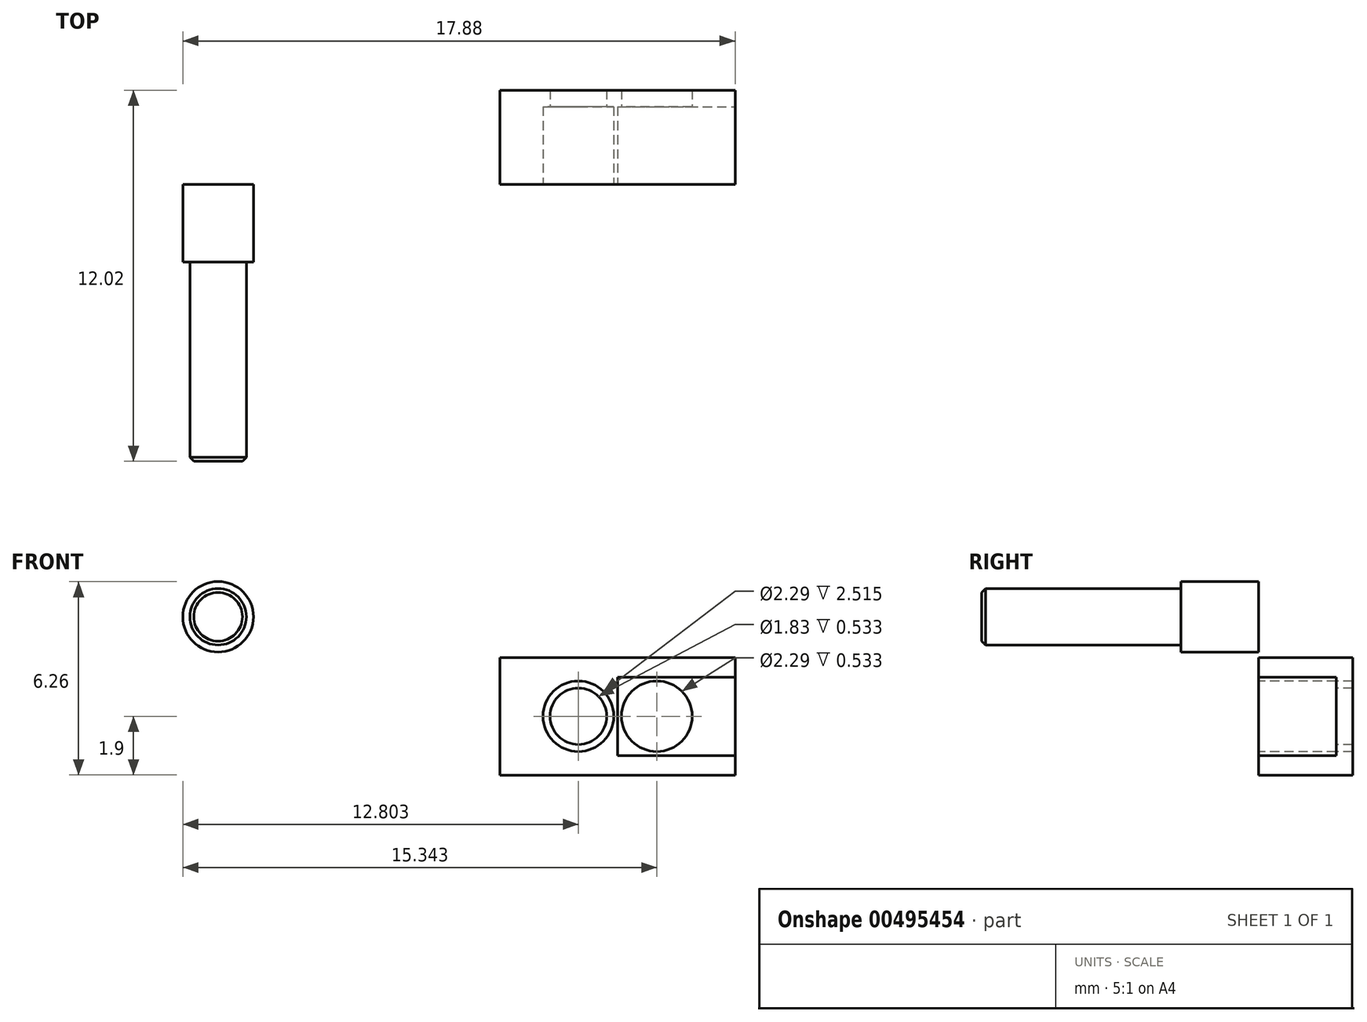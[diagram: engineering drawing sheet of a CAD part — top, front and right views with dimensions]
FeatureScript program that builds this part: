
annotation { "Feature Type Name" : "Feature", "Feature Type Description" : "" }
export const myFeature = defineFeature(function(context is Context, id is Id, definition is map)
    precondition{}
    {
        {
            var Q0;
            Q0=qCreatedBy(makeId("Front.planeOp"),FACE);
            var sketch = newSketch(context, id + "F0", { "sketchPlane" : qUnion([Q0])});
            skCircle(sketch, "E0", {"center": v(-24.36, 19.51) * mm, "radius": 0.91 * mm});
            skCircle(sketch, "E1", {"center": v(-24.36, 19.51) * mm, "radius": 1.14 * mm});
            skSolve(sketch);
        }
        {
            var Q0;
            Q0=makeQuery(id+"F0.imprint","IMPRINT",FACE,{"disambiguationData":[TD([[makeQuery(id+"F0.imprint","IMPRINT",EDGE,{"derivedFrom":sQuery(id+"F0.wireOp",EDGE,"E0")}),1.0]])]});
            extrude(context, id + "F1", {"entities" : qUnion([Q0]), "depth" : 8.97 * mm});
        }
        {
            var Q0;
            Q0 = qSketchRegion(id + "F0", true);
            extrude(context, id + "F2", {"entities" : qUnion([Q0]), "operationType" : NewBodyOperationType.ADD, "depth" : 2.5 * mm});
        }
        {
            var Q0;
            Q0=makeQuery(id+"F1.opExtrude","CAP_EDGE",EDGE,{"disambiguationData":[OSD([sQuery(id+"F0.wireOp",EDGE,"E0")])],"isStart":false});
            chamfer(context, id + "F3", {"entities" : qUnion([Q0]), "width" : 0.13 * mm, "tangentPropagation" : true});
        }
        {
            var Q0;
            Q0=qCreatedBy(makeId("Front.planeOp"),FACE);
            var sketch = newSketch(context, id + "F4", { "sketchPlane" : qUnion([Q0])});
            skLineSegment(sketch, "E2.bottom", {"start": v(-15.24, 18.2) * mm, "end": v(-7.62, 18.2) * mm});
            skLineSegment(sketch, "E2.top", {"start": v(-15.24, 14.39) * mm, "end": v(-7.62, 14.39) * mm});
            skLineSegment(sketch, "E2.left", {"start": v(-15.24, 18.2) * mm, "end": v(-15.24, 14.39) * mm});
            skLineSegment(sketch, "E2.right", {"start": v(-7.62, 18.2) * mm, "end": v(-7.62, 14.39) * mm});
            skCircle(sketch, "E3", {"center": v(-12.7, 16.3) * mm, "radius": 0.91 * mm});
            skCircle(sketch, "E4", {"center": v(-12.7, 16.3) * mm, "radius": 1.14 * mm});
            skLineSegment(sketch, "E5", {"start": v(-11.43, 18.2) * mm, "end": v(-11.43, 14.39) * mm});
            skCircle(sketch, "E6.MirrorC", {"center": v(-10.16, 16.3) * mm, "radius": 1.14 * mm});
            skCircle(sketch, "E7.MirrorC", {"center": v(-10.16, 16.3) * mm, "radius": 0.91 * mm});
            skLineSegment(sketch, "E8", {"start": v(-15.24, 17.56) * mm, "end": v(-7.62, 17.56) * mm});
            skLineSegment(sketch, "E9", {"start": v(-15.24, 15.02) * mm, "end": v(-7.62, 15.02) * mm});
            skSolve(sketch);
        }
        {
            var Q0;
            {var subQ0=sQuery(id+"F4.wireOp",EDGE,"E2.left");var subQ1=sQuery(id+"F4.wireOp",EDGE,"E2.bottom");var subQ2=makeQuery(id+"F4.imprint","INTERSECT",VERTEX,{"derivedFrom":[subQ1,subQ0]});Q0=makeQuery(id+"F4.imprint","IMPRINT",FACE,{"disambiguationData":[TD([[makeQuery(id+"F4.imprint","IMPRINT",EDGE,{"disambiguationData":[TD([[subQ2,-1.0]])],"derivedFrom":subQ1}),-1.0]])]});}
            var Q1;
            {var subQ0=sQuery(id+"F4.wireOp",EDGE,"E2.right");var subQ1=sQuery(id+"F4.wireOp",EDGE,"E2.bottom");var subQ2=makeQuery(id+"F4.imprint","INTERSECT",VERTEX,{"derivedFrom":[subQ1,subQ0]});Q1=makeQuery(id+"F4.imprint","IMPRINT",FACE,{"disambiguationData":[TD([[makeQuery(id+"F4.imprint","IMPRINT",EDGE,{"disambiguationData":[TD([[subQ2,1.0]])],"derivedFrom":subQ1}),-1.0]])]});}
            var Q2;
            Q2=makeQuery(id+"F4.imprint","IMPRINT",FACE,{"disambiguationData":[TD([[makeQuery(id+"F4.imprint","IMPRINT",EDGE,{"derivedFrom":sQuery(id+"F4.wireOp",EDGE,"E6.MirrorC")}),1.0]])]});
            var Q3;
            Q3=makeQuery(id+"F4.imprint","IMPRINT",FACE,{"disambiguationData":[TD([[makeQuery(id+"F4.imprint","IMPRINT",EDGE,{"derivedFrom":sQuery(id+"F4.wireOp",EDGE,"E4")}),-1.0]])]});
            var Q4;
            Q4=makeQuery(id+"F4.imprint","IMPRINT",FACE,{"disambiguationData":[TD([[makeQuery(id+"F4.imprint","IMPRINT",EDGE,{"derivedFrom":sQuery(id+"F4.wireOp",EDGE,"E3")}),-1.0]])]});
            var Q5;
            Q5=makeQuery(id+"F4.imprint","IMPRINT",FACE,{"disambiguationData":[TD([[makeQuery(id+"F4.imprint","IMPRINT",EDGE,{"derivedFrom":sQuery(id+"F4.wireOp",EDGE,"E3")}),1.0]])]});
            var Q6;
            Q6=makeQuery(id+"F4.imprint","IMPRINT",FACE,{"disambiguationData":[TD([[makeQuery(id+"F4.imprint","IMPRINT",EDGE,{"derivedFrom":sQuery(id+"F4.wireOp",EDGE,"E7.MirrorC")}),-1.0]])]});
            var Q7;
            Q7=makeQuery(id+"F4.imprint","IMPRINT",FACE,{"disambiguationData":[TD([[makeQuery(id+"F4.imprint","IMPRINT",EDGE,{"derivedFrom":sQuery(id+"F4.wireOp",EDGE,"E6.MirrorC")}),-1.0]])]});
            var Q8;
            {var subQ0=sQuery(id+"F4.wireOp",EDGE,"E2.left");var subQ1=sQuery(id+"F4.wireOp",EDGE,"E2.top");var subQ2=makeQuery(id+"F4.imprint","INTERSECT",VERTEX,{"derivedFrom":[subQ1,subQ0]});Q8=makeQuery(id+"F4.imprint","IMPRINT",FACE,{"disambiguationData":[TD([[makeQuery(id+"F4.imprint","IMPRINT",EDGE,{"disambiguationData":[TD([[subQ2,-1.0]])],"derivedFrom":subQ1}),1.0]])]});}
            var Q9;
            {var subQ0=sQuery(id+"F4.wireOp",EDGE,"E2.right");var subQ1=sQuery(id+"F4.wireOp",EDGE,"E2.top");var subQ2=makeQuery(id+"F4.imprint","INTERSECT",VERTEX,{"derivedFrom":[subQ1,subQ0]});Q9=makeQuery(id+"F4.imprint","IMPRINT",FACE,{"disambiguationData":[TD([[makeQuery(id+"F4.imprint","IMPRINT",EDGE,{"disambiguationData":[TD([[subQ2,1.0]])],"derivedFrom":subQ1}),1.0]])]});}
            extrude(context, id + "F5", {"entities" : qUnion([Q0, Q1, Q2, Q3, Q4, Q5, Q6, Q7, Q8, Q9]), "oppositeDirection" : true, "depth" : 3.05 * mm});
        }
        {
            var Q0;
            Q0=makeQuery(id+"F4.imprint","IMPRINT",FACE,{"disambiguationData":[TD([[makeQuery(id+"F4.imprint","IMPRINT",EDGE,{"derivedFrom":sQuery(id+"F4.wireOp",EDGE,"E3")}),-1.0]])]});
            var Q1;
            Q1=makeQuery(id+"F4.imprint","IMPRINT",FACE,{"disambiguationData":[TD([[makeQuery(id+"F4.imprint","IMPRINT",EDGE,{"derivedFrom":sQuery(id+"F4.wireOp",EDGE,"E6.MirrorC")}),-1.0]])]});
            extrude(context, id + "F6", {"entities" : qUnion([Q0, Q1]), "operationType" : NewBodyOperationType.REMOVE, "oppositeDirection" : true, "depth" : 2.5 * mm});
        }
        {
            var Q0;
            Q0=makeQuery(id+"F4.imprint","IMPRINT",FACE,{"disambiguationData":[TD([[makeQuery(id+"F4.imprint","IMPRINT",EDGE,{"derivedFrom":sQuery(id+"F4.wireOp",EDGE,"E3")}),1.0]])]});
            var Q1;
            Q1=makeQuery(id+"F4.imprint","IMPRINT",FACE,{"disambiguationData":[TD([[makeQuery(id+"F4.imprint","IMPRINT",EDGE,{"derivedFrom":sQuery(id+"F4.wireOp",EDGE,"E7.MirrorC")}),-1.0]])]});
            extrude(context, id + "F7", {"entities" : qUnion([Q0, Q1]), "operationType" : NewBodyOperationType.REMOVE, "oppositeDirection" : true, "depth" : 3.05 * mm});
        }
    });
